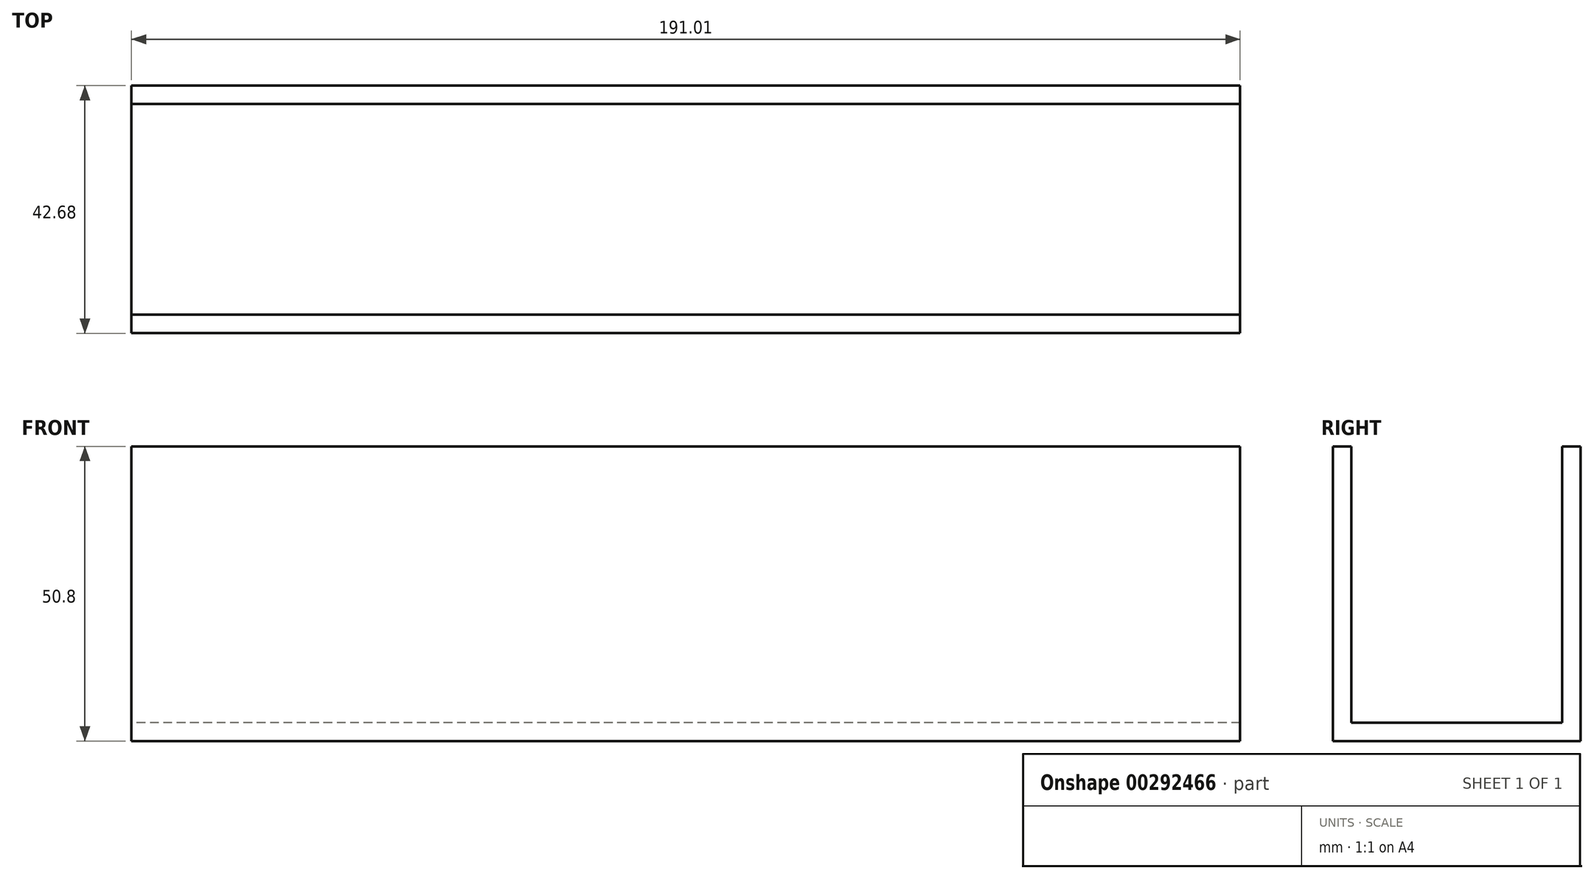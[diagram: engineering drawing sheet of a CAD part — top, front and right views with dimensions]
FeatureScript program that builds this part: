
annotation { "Feature Type Name" : "Feature", "Feature Type Description" : "" }
export const myFeature = defineFeature(function(context is Context, id is Id, definition is map)
    precondition{}
    {
        {
            var Q0;
            Q0=qCreatedBy(makeId("Front.planeOp"),FACE);
            var sketch = newSketch(context, id + "F0", { "sketchPlane" : qUnion([Q0])});
            skLineSegment(sketch, "E0", {"start": v(0, 0) * mm, "end": v(191, 0) * mm});
            skLineSegment(sketch, "E1", {"start": v(191, 0) * mm, "end": v(191, 50.8) * mm});
            skLineSegment(sketch, "E2", {"start": v(191, 50.8) * mm, "end": v(0, 50.8) * mm});
            skLineSegment(sketch, "E3", {"start": v(0, 50.8) * mm, "end": v(0, 0) * mm});
            skSolve(sketch);
        }
        {
            var Q0;
            Q0=makeQuery(id+"F0.imprint","IMPRINT",FACE,{"disambiguationData":[TD([[makeQuery(id+"F0.imprint","IMPRINT",EDGE,{"derivedFrom":sQuery(id+"F0.wireOp",EDGE,"E0")}),1.0]])]});
            extrude(context, id + "F1", {"entities" : qUnion([Q0]), "endBound" : BoundingType.SYMMETRIC, "depth" : 42.67 * mm});
        }
        {
            var Q0;
            Q0=qCreatedBy(makeId("Right.planeOp"),FACE);
            var sketch = newSketch(context, id + "F2", { "sketchPlane" : qUnion([Q0])});
            skLineSegment(sketch, "E4.bottom", {"start": v(-18.16, 50.8) * mm, "end": v(18.16, 50.8) * mm});
            skLineSegment(sketch, "E4.top", {"start": v(-18.16, 3.18) * mm, "end": v(18.16, 3.18) * mm});
            skLineSegment(sketch, "E4.left", {"start": v(-18.16, 50.8) * mm, "end": v(-18.16, 3.18) * mm});
            skLineSegment(sketch, "E4.right", {"start": v(18.16, 50.8) * mm, "end": v(18.16, 3.18) * mm});
            skSolve(sketch);
        }
        {
            var Q0;
            Q0 = qSketchRegion(id + "F2", true);
            extrude(context, id + "F3", {"entities" : qUnion([Q0]), "operationType" : NewBodyOperationType.REMOVE, "endBound" : BoundingType.THROUGH_ALL, "depth" : 25.4 * mm});
        }
    });
